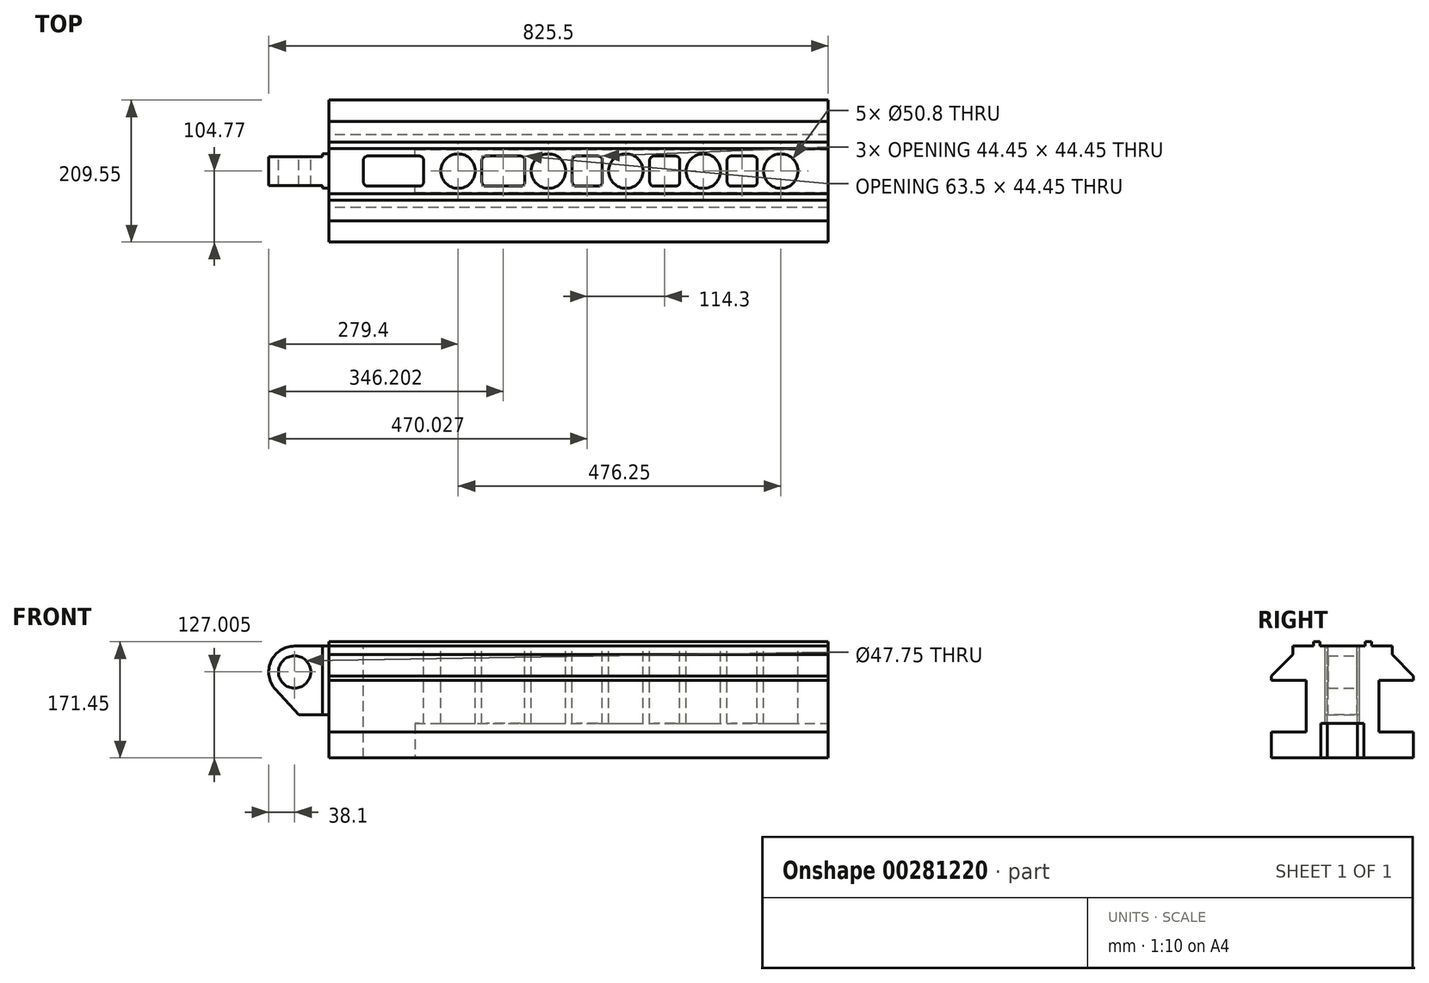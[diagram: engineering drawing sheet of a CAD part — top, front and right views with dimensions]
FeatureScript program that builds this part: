
annotation { "Feature Type Name" : "Feature", "Feature Type Description" : "" }
export const myFeature = defineFeature(function(context is Context, id is Id, definition is map)
    precondition{}
    {
        {
            var Q0;
            Q0=qCreatedBy(makeId("Right.planeOp"),FACE);
            var sketch = newSketch(context, id + "F0", { "sketchPlane" : qUnion([Q0])});
            skLineSegment(sketch, "E0.bottom", {"start": v(-42.8, 85.72) * mm, "end": v(-33.27, 85.72) * mm});
            skLineSegment(sketch, "E0.top", {"start": v(-104.78, -85.73) * mm, "end": v(104.77, -85.73) * mm});
            skLineSegment(sketch, "E0.left", {"start": v(-104.77, 85.72) * mm, "end": v(-104.78, 28.57) * mm});
            skLineSegment(sketch, "E0.right", {"start": v(104.78, 85.72) * mm, "end": v(104.78, 28.58) * mm});
            skPoint(sketch, "E0.middle", {"position": v(0, 0) * mm});
            skLineSegment(sketch, "E1.0", {"start": v(-104.77, 79.38) * mm, "end": v(-42.8, 79.38) * mm});
            skLineSegment(sketch, "E2", {"start": v(0, 110.93) * mm, "end": v(0, 53.07) * mm});
            skLineSegment(sketch, "E3.0", {"start": v(-33.27, 85.72) * mm, "end": v(-33.27, 79.38) * mm});
            skLineSegment(sketch, "E4.0", {"start": v(-42.8, 85.72) * mm, "end": v(-42.8, 79.38) * mm});
            skLineSegment(sketch, "E5.MirrorCS", {"start": v(42.8, 85.72) * mm, "end": v(42.8, 79.38) * mm});
            skLineSegment(sketch, "E6.MirrorCS", {"start": v(33.27, 85.72) * mm, "end": v(33.27, 79.38) * mm});
            skPoint(sketch, "E7.orphan", {"position": v(-42.8, 53.07) * mm});
            skPoint(sketch, "E8.orphan", {"position": v(-33.27, 53.07) * mm});
            skPoint(sketch, "E9.orphan", {"position": v(33.27, 53.07) * mm});
            skPoint(sketch, "E10.orphan", {"position": v(42.8, 53.07) * mm});
            skLineSegment(sketch, "E11.trimOffspring", {"start": v(33.27, 85.72) * mm, "end": v(42.8, 85.72) * mm});
            skPoint(sketch, "E12.orphan", {"position": v(-33.27, 110.93) * mm});
            skPoint(sketch, "E13.orphan", {"position": v(-42.8, 110.93) * mm});
            skPoint(sketch, "E14.orphan", {"position": v(33.27, 110.93) * mm});
            skPoint(sketch, "E15.orphan", {"position": v(42.8, 110.93) * mm});
            skLineSegment(sketch, "E16.trimOffspring", {"start": v(42.8, 79.38) * mm, "end": v(104.78, 79.38) * mm});
            skLineSegment(sketch, "E17.trimOffspring", {"start": v(-33.27, 79.38) * mm, "end": v(33.27, 79.38) * mm});
            skLineSegment(sketch, "E18.0", {"start": v(42.8, 28.57) * mm, "end": v(104.78, 28.57) * mm});
            skLineSegment(sketch, "E19.0", {"start": v(42.8, -47.62) * mm, "end": v(104.78, -47.62) * mm});
            skLineSegment(sketch, "E20.0", {"start": v(53.85, 28.57) * mm, "end": v(53.85, -47.62) * mm});
            skLineSegment(sketch, "E21.trimOffspring", {"start": v(104.77, -47.62) * mm, "end": v(104.77, -85.73) * mm});
            skLineSegment(sketch, "E22.MirrorCS", {"start": v(-42.8, -47.62) * mm, "end": v(-104.78, -47.62) * mm});
            skLineSegment(sketch, "E23.MirrorCS", {"start": v(-42.8, 28.57) * mm, "end": v(-104.78, 28.57) * mm});
            skLineSegment(sketch, "E24.MirrorCS", {"start": v(-53.85, 28.57) * mm, "end": v(-53.85, -47.62) * mm});
            skLineSegment(sketch, "E25.trimOffspring", {"start": v(-104.78, -47.62) * mm, "end": v(-104.78, -85.73) * mm});
            skSolve(sketch);
        }
        {
            var Q0;
            Q0 = qSketchRegion(id + "F0", true);
            extrude(context, id + "F1", {"entities" : qUnion([Q0]), "endBound" : BoundingType.SYMMETRIC, "depth" : 736.6 * mm});
        }
        {
            var Q0;
            Q0=makeQuery(id+"F1.opExtrude","CAP_FACE",FACE,{"disambiguationData":[OSD([sQuery(id+"F0.wireOp",EDGE,"E0.bottom"),sQuery(id+"F0.wireOp",EDGE,"E0.top"),sQuery(id+"F0.wireOp",EDGE,"E0.left"),sQuery(id+"F0.wireOp",EDGE,"E0.right"),sQuery(id+"F0.wireOp",EDGE,"E1.0"),sQuery(id+"F0.wireOp",EDGE,"E3.0"),sQuery(id+"F0.wireOp",EDGE,"E4.0"),sQuery(id+"F0.wireOp",EDGE,"E5.MirrorCS"),sQuery(id+"F0.wireOp",EDGE,"E6.MirrorCS"),sQuery(id+"F0.wireOp",EDGE,"E11.trimOffspring"),sQuery(id+"F0.wireOp",EDGE,"E16.trimOffspring"),sQuery(id+"F0.wireOp",EDGE,"E17.trimOffspring"),sQuery(id+"F0.wireOp",EDGE,"E18.0"),sQuery(id+"F0.wireOp",EDGE,"E19.0"),sQuery(id+"F0.wireOp",EDGE,"E20.0"),sQuery(id+"F0.wireOp",EDGE,"E21.trimOffspring"),sQuery(id+"F0.wireOp",EDGE,"E22.MirrorCS"),sQuery(id+"F0.wireOp",EDGE,"E23.MirrorCS"),sQuery(id+"F0.wireOp",EDGE,"E24.MirrorCS"),sQuery(id+"F0.wireOp",EDGE,"E25.trimOffspring")])],"isStart":false});
            var sketch = newSketch(context, id + "F2", { "sketchPlane" : qUnion([Q0])});
            skLineSegment(sketch, "E26.0", {"start": v(-104.78, -85.73) * mm, "end": v(104.77, -85.73) * mm, "construction": true});
            skLineSegment(sketch, "E27.bottom", {"start": v(-31.75, -34.93) * mm, "end": v(31.75, -34.93) * mm});
            skLineSegment(sketch, "E27.top", {"start": v(-31.75, -136.53) * mm, "end": v(31.75, -136.53) * mm});
            skLineSegment(sketch, "E27.left", {"start": v(-31.75, -34.93) * mm, "end": v(-31.75, -136.53) * mm});
            skLineSegment(sketch, "E27.right", {"start": v(31.75, -34.93) * mm, "end": v(31.75, -136.53) * mm});
            skPoint(sketch, "E27.middle", {"position": v(0, -85.73) * mm});
            skSolve(sketch);
        }
        {
            var Q0;
            Q0 = qSketchRegion(id + "F2", true);
            extrude(context, id + "F3", {"entities" : qUnion([Q0]), "operationType" : NewBodyOperationType.REMOVE, "oppositeDirection" : true, "depth" : 609.6 * mm});
        }
        {
            var Q0;
            Q0=makeQuery(id+"F1.opExtrude","SWEPT_FACE",FACE,{"disambiguationData":[OSD([sQuery(id+"F0.wireOp",EDGE,"E17.trimOffspring")])]});
            var sketch = newSketch(context, id + "F4", { "sketchPlane" : qUnion([Q0])});
            skLineSegment(sketch, "E28.0", {"start": v(-368.3, -33.27) * mm, "end": v(-368.3, 33.27) * mm, "construction": true});
            skLineSegment(sketch, "E29.0", {"start": v(-177.8, -33.27) * mm, "end": v(-177.8, 33.27) * mm, "construction": true});
            skLineSegment(sketch, "E30.0", {"start": v(-44.45, -33.27) * mm, "end": v(-44.45, 33.27) * mm, "construction": true});
            skLineSegment(sketch, "E31.0", {"start": v(69.85, -33.27) * mm, "end": v(69.85, 33.27) * mm, "construction": true});
            skLineSegment(sketch, "E32.0", {"start": v(184.15, -33.27) * mm, "end": v(184.15, 33.27) * mm, "construction": true});
            skLineSegment(sketch, "E33.0", {"start": v(298.45, -33.27) * mm, "end": v(298.45, 33.27) * mm, "construction": true});
            skLineSegment(sketch, "E34", {"start": v(-368.3, 0) * mm, "end": v(340.6, 0) * mm, "construction": true});
            skPoint(sketch, "E35", {"position": v(-177.8, 0) * mm});
            skPoint(sketch, "E36", {"position": v(-44.45, 0) * mm});
            skPoint(sketch, "E37", {"position": v(69.85, 0) * mm});
            skPoint(sketch, "E38", {"position": v(184.15, 0) * mm});
            skPoint(sketch, "E39", {"position": v(298.45, 0) * mm});
            skSolve(sketch);
        }
        {
            var Q0;
            Q0=sQuery(id+"F4.wireOp",VERTEX,"E35");
            var Q1;
            Q1=sQuery(id+"F4.wireOp",VERTEX,"E36");
            var Q2;
            Q2=sQuery(id+"F4.wireOp",VERTEX,"E37");
            var Q3;
            Q3=sQuery(id+"F4.wireOp",VERTEX,"E38");
            var Q4;
            Q4=sQuery(id+"F4.wireOp",VERTEX,"E39");
            var Q5;
            Q5=makeQuery(id+"F1.opExtrude","SWEPT_BODY",BODY,{"disambiguationData":[OSD([sQuery(id+"F0.wireOp",EDGE,"E0.bottom"),sQuery(id+"F0.wireOp",EDGE,"E0.top"),sQuery(id+"F0.wireOp",EDGE,"E0.left"),sQuery(id+"F0.wireOp",EDGE,"E0.right"),sQuery(id+"F0.wireOp",EDGE,"E1.0"),sQuery(id+"F0.wireOp",EDGE,"E3.0"),sQuery(id+"F0.wireOp",EDGE,"E4.0"),sQuery(id+"F0.wireOp",EDGE,"E5.MirrorCS"),sQuery(id+"F0.wireOp",EDGE,"E6.MirrorCS"),sQuery(id+"F0.wireOp",EDGE,"E11.trimOffspring"),sQuery(id+"F0.wireOp",EDGE,"E16.trimOffspring"),sQuery(id+"F0.wireOp",EDGE,"E17.trimOffspring"),sQuery(id+"F0.wireOp",EDGE,"E18.0"),sQuery(id+"F0.wireOp",EDGE,"E19.0"),sQuery(id+"F0.wireOp",EDGE,"E20.0"),sQuery(id+"F0.wireOp",EDGE,"E21.trimOffspring"),sQuery(id+"F0.wireOp",EDGE,"E22.MirrorCS"),sQuery(id+"F0.wireOp",EDGE,"E23.MirrorCS"),sQuery(id+"F0.wireOp",EDGE,"E24.MirrorCS"),sQuery(id+"F0.wireOp",EDGE,"E25.trimOffspring")])]});
            hole(context, id + "F5", {"style" : HoleStyle.SIMPLE, "endStyle" : HoleEndStyle.THROUGH, "holeDiameter" : 50.8 * mm, "tappedDepth" : 42.34 * mm, "tapClearance" : 3, "startFromSketch" : true, "locations" : qUnion([Q0, Q1, Q2, Q3, Q4]), "scope" : qUnion([Q5])});
        }
        {
            var Q0;
            Q0=makeQuery(id+"F1.opExtrude","SWEPT_FACE",FACE,{"disambiguationData":[OSD([sQuery(id+"F0.wireOp",EDGE,"E17.trimOffspring")])]});
            var sketch = newSketch(context, id + "F6", { "sketchPlane" : qUnion([Q0])});
            skCircle(sketch, "E40.0", {"center": v(-177.8, 0) * mm, "radius": 25.4 * mm, "construction": true});
            skCircle(sketch, "E41.0", {"center": v(-44.45, 0) * mm, "radius": 25.4 * mm, "construction": true});
            skCircle(sketch, "E42.0", {"center": v(69.85, 0) * mm, "radius": 25.4 * mm, "construction": true});
            skCircle(sketch, "E43.0", {"center": v(184.15, 0) * mm, "radius": 25.4 * mm, "construction": true});
            skCircle(sketch, "E44.0", {"center": v(298.45, 0) * mm, "radius": 25.4 * mm, "construction": true});
            skLineSegment(sketch, "E45", {"start": v(298.45, 130.35) * mm, "end": v(298.45, -144.63) * mm, "construction": true});
            skLineSegment(sketch, "E46", {"start": v(184.15, 135.32) * mm, "end": v(184.15, -149.6) * mm, "construction": true});
            skLineSegment(sketch, "E47", {"start": v(0, 0) * mm, "end": v(382.37, 0) * mm, "construction": true});
            skPoint(sketch, "E47.endSnap0", {"position": v(368.3, 0) * mm});
            skLineSegment(sketch, "E48.bottom", {"start": v(225.55, 22.23) * mm, "end": v(257.3, 22.23) * mm});
            skLineSegment(sketch, "E48.top", {"start": v(225.55, -22.23) * mm, "end": v(257.3, -22.23) * mm});
            skLineSegment(sketch, "E48.left", {"start": v(219.2, 15.88) * mm, "end": v(219.2, -15.88) * mm});
            skLineSegment(sketch, "E48.right", {"start": v(263.65, 15.88) * mm, "end": v(263.65, -15.88) * mm});
            skPoint(sketch, "E49.visualSharp", {"position": v(219.2, 22.23) * mm});
            skArc(sketch, "E49.filletArc", {"start": v(225.55, 22.23) * mm, "mid": v(221.06, 20.37) * mm, "end": v(219.2, 15.88) * mm});
            skPoint(sketch, "E50.visualSharp", {"position": v(263.65, 22.23) * mm});
            skArc(sketch, "E50.filletArc", {"start": v(263.65, 15.88) * mm, "mid": v(261.8, 20.37) * mm, "end": v(257.3, 22.23) * mm});
            skPoint(sketch, "E51.visualSharp", {"position": v(263.65, -22.23) * mm});
            skArc(sketch, "E51.filletArc", {"start": v(257.3, -22.23) * mm, "mid": v(261.8, -20.37) * mm, "end": v(263.65, -15.88) * mm});
            skPoint(sketch, "E52.visualSharp", {"position": v(219.2, -22.23) * mm});
            skArc(sketch, "E52.filletArc", {"start": v(219.2, -15.88) * mm, "mid": v(221.06, -20.37) * mm, "end": v(225.55, -22.22) * mm});
            skPoint(sketch, "E53.1.0.0", {"position": v(149.35, 22.23) * mm});
            skPoint(sketch, "E53.1.0.1", {"position": v(149.35, -22.23) * mm});
            skLineSegment(sketch, "E53.1.0.2", {"start": v(149.35, 15.88) * mm, "end": v(149.35, -15.88) * mm});
            skLineSegment(sketch, "E53.1.0.3", {"start": v(104.9, 15.88) * mm, "end": v(104.9, -15.88) * mm});
            skLineSegment(sketch, "E53.1.0.4", {"start": v(111.25, -22.23) * mm, "end": v(143, -22.23) * mm});
            skLineSegment(sketch, "E53.1.0.5", {"start": v(111.25, 22.23) * mm, "end": v(143, 22.23) * mm});
            skPoint(sketch, "E53.1.0.6", {"position": v(104.9, 22.23) * mm});
            skPoint(sketch, "E53.1.0.7", {"position": v(104.9, -22.23) * mm});
            skArc(sketch, "E53.1.0.8", {"start": v(149.35, 15.88) * mm, "mid": v(147.5, 20.37) * mm, "end": v(143, 22.23) * mm});
            skArc(sketch, "E53.1.0.9", {"start": v(104.9, -15.88) * mm, "mid": v(106.76, -20.37) * mm, "end": v(111.25, -22.22) * mm});
            skArc(sketch, "E53.1.0.10", {"start": v(111.25, 22.23) * mm, "mid": v(106.76, 20.37) * mm, "end": v(104.9, 15.88) * mm});
            skArc(sketch, "E53.1.0.11", {"start": v(143, -22.23) * mm, "mid": v(147.5, -20.37) * mm, "end": v(149.35, -15.88) * mm});
            skPoint(sketch, "E53.2.0.0", {"position": v(35.05, 22.23) * mm});
            skPoint(sketch, "E53.2.0.1", {"position": v(35.05, -22.23) * mm});
            skLineSegment(sketch, "E53.2.0.2", {"start": v(35.05, 15.88) * mm, "end": v(35.05, -15.88) * mm});
            skLineSegment(sketch, "E53.2.0.3", {"start": v(-9.4, 15.88) * mm, "end": v(-9.4, -15.88) * mm});
            skLineSegment(sketch, "E53.2.0.4", {"start": v(-3.05, -22.23) * mm, "end": v(28.7, -22.23) * mm});
            skLineSegment(sketch, "E53.2.0.5", {"start": v(-3.05, 22.23) * mm, "end": v(28.7, 22.23) * mm});
            skPoint(sketch, "E53.2.0.6", {"position": v(-9.4, 22.23) * mm});
            skPoint(sketch, "E53.2.0.7", {"position": v(-9.4, -22.23) * mm});
            skArc(sketch, "E53.2.0.8", {"start": v(35.05, 15.88) * mm, "mid": v(33.2, 20.37) * mm, "end": v(28.7, 22.23) * mm});
            skArc(sketch, "E53.2.0.9", {"start": v(-9.4, -15.88) * mm, "mid": v(-7.54, -20.37) * mm, "end": v(-3.05, -22.22) * mm});
            skArc(sketch, "E53.2.0.10", {"start": v(-3.05, 22.23) * mm, "mid": v(-7.54, 20.37) * mm, "end": v(-9.4, 15.88) * mm});
            skArc(sketch, "E53.2.0.11", {"start": v(28.7, -22.23) * mm, "mid": v(33.2, -20.37) * mm, "end": v(35.05, -15.88) * mm});
            skPoint(sketch, "E53.3.0.0", {"position": v(-79.25, 22.23) * mm});
            skPoint(sketch, "E53.3.0.1", {"position": v(-79.25, -22.23) * mm});
            skLineSegment(sketch, "E53.3.0.2", {"start": v(-79.25, 15.88) * mm, "end": v(-79.25, -15.87) * mm});
            skLineSegment(sketch, "E53.3.0.3", {"start": v(-142.75, 15.88) * mm, "end": v(-142.75, -15.88) * mm});
            skLineSegment(sketch, "E53.3.0.4", {"start": v(-136.4, -22.22) * mm, "end": v(-85.6, -22.22) * mm});
            skLineSegment(sketch, "E53.3.0.5", {"start": v(-136.4, 22.23) * mm, "end": v(-85.6, 22.23) * mm});
            skPoint(sketch, "E53.3.0.6", {"position": v(-123.7, 22.23) * mm});
            skPoint(sketch, "E53.3.0.7", {"position": v(-123.7, -22.23) * mm});
            skArc(sketch, "E53.3.0.9", {"start": v(-142.75, -15.88) * mm, "mid": v(-140.89, -20.37) * mm, "end": v(-136.4, -22.22) * mm});
            skArc(sketch, "E53.3.0.10", {"start": v(-136.4, 22.23) * mm, "mid": v(-140.89, 20.37) * mm, "end": v(-142.75, 15.88) * mm});
            skPoint(sketch, "E53.4.0.0", {"position": v(-193.55, 22.23) * mm});
            skPoint(sketch, "E53.4.0.1", {"position": v(-193.55, -22.23) * mm});
            skLineSegment(sketch, "E53.4.0.2", {"start": v(-228.6, 15.88) * mm, "end": v(-228.6, -15.88) * mm});
            skLineSegment(sketch, "E53.4.0.3", {"start": v(-317.5, 15.87) * mm, "end": v(-317.5, -15.88) * mm});
            skLineSegment(sketch, "E53.4.0.4", {"start": v(-311.15, -22.22) * mm, "end": v(-234.95, -22.22) * mm});
            skLineSegment(sketch, "E53.4.0.5", {"start": v(-311.15, 22.22) * mm, "end": v(-234.95, 22.22) * mm});
            skPoint(sketch, "E53.4.0.6", {"position": v(-238, 22.23) * mm});
            skPoint(sketch, "E53.4.0.7", {"position": v(-238, -22.23) * mm});
            skArc(sketch, "E53.4.0.9", {"start": v(-317.5, -15.88) * mm, "mid": v(-315.64, -20.37) * mm, "end": v(-311.15, -22.22) * mm});
            skArc(sketch, "E53.4.0.10", {"start": v(-311.15, 22.22) * mm, "mid": v(-315.64, 20.37) * mm, "end": v(-317.5, 15.87) * mm});
            skLineSegment(sketch, "E53.direction1", {"start": v(263.65, 22.23) * mm, "end": v(149.35, 22.23) * mm, "construction": true});
            skArc(sketch, "E54.filletArc", {"start": v(-79.25, 15.88) * mm, "mid": v(-81.1, 20.37) * mm, "end": v(-85.6, 22.23) * mm});
            skPoint(sketch, "E55.visualSharp", {"position": v(-79.25, -22.22) * mm});
            skArc(sketch, "E55.filletArc", {"start": v(-85.6, -22.22) * mm, "mid": v(-81.1, -20.37) * mm, "end": v(-79.25, -15.87) * mm});
            skPoint(sketch, "E56.visualSharp", {"position": v(-228.6, 22.22) * mm});
            skArc(sketch, "E56.filletArc", {"start": v(-228.6, 15.88) * mm, "mid": v(-230.46, 20.37) * mm, "end": v(-234.95, 22.22) * mm});
            skPoint(sketch, "E57.visualSharp", {"position": v(-228.6, -22.22) * mm});
            skArc(sketch, "E57.filletArc", {"start": v(-234.95, -22.23) * mm, "mid": v(-230.46, -20.37) * mm, "end": v(-228.6, -15.88) * mm});
            skSolve(sketch);
        }
        {
            var Q0;
            Q0 = qSketchRegion(id + "F6", true);
            extrude(context, id + "F7", {"entities" : qUnion([Q0]), "operationType" : NewBodyOperationType.REMOVE, "endBound" : BoundingType.THROUGH_ALL, "oppositeDirection" : true, "depth" : 25.4 * mm});
        }
        {
            var Q0;
            Q0=makeQuery(id+"F1.opExtrude","CAP_FACE",FACE,{"disambiguationData":[OSD([sQuery(id+"F0.wireOp",EDGE,"E0.bottom"),sQuery(id+"F0.wireOp",EDGE,"E0.top"),sQuery(id+"F0.wireOp",EDGE,"E0.left"),sQuery(id+"F0.wireOp",EDGE,"E0.right"),sQuery(id+"F0.wireOp",EDGE,"E1.0"),sQuery(id+"F0.wireOp",EDGE,"E3.0"),sQuery(id+"F0.wireOp",EDGE,"E4.0"),sQuery(id+"F0.wireOp",EDGE,"E5.MirrorCS"),sQuery(id+"F0.wireOp",EDGE,"E6.MirrorCS"),sQuery(id+"F0.wireOp",EDGE,"E11.trimOffspring"),sQuery(id+"F0.wireOp",EDGE,"E16.trimOffspring"),sQuery(id+"F0.wireOp",EDGE,"E17.trimOffspring"),sQuery(id+"F0.wireOp",EDGE,"E18.0"),sQuery(id+"F0.wireOp",EDGE,"E19.0"),sQuery(id+"F0.wireOp",EDGE,"E20.0"),sQuery(id+"F0.wireOp",EDGE,"E21.trimOffspring"),sQuery(id+"F0.wireOp",EDGE,"E22.MirrorCS"),sQuery(id+"F0.wireOp",EDGE,"E23.MirrorCS"),sQuery(id+"F0.wireOp",EDGE,"E24.MirrorCS"),sQuery(id+"F0.wireOp",EDGE,"E25.trimOffspring")])],"isStart":false});
            var sketch = newSketch(context, id + "F8", { "sketchPlane" : qUnion([Q0])});
            skLineSegment(sketch, "E58", {"start": v(0, 182.5) * mm, "end": v(0, -180.71) * mm, "construction": true});
            skPoint(sketch, "E58.endSnap0", {"position": v(0, -34.93) * mm});
            skLineSegment(sketch, "E59.0", {"start": v(-73.15, 182.5) * mm, "end": v(-73.15, -180.71) * mm, "construction": true});
            skLineSegment(sketch, "E60.0", {"start": v(-104.77, 66.67) * mm, "end": v(-42.8, 66.67) * mm, "construction": true});
            skLineSegment(sketch, "E61", {"start": v(-73.15, 66.67) * mm, "end": v(-123, 16.84) * mm});
            skLineSegment(sketch, "E62", {"start": v(-73.15, 66.67) * mm, "end": v(-73.15, 82.75) * mm});
            skLineSegment(sketch, "E63", {"start": v(-73.15, 82.75) * mm, "end": v(-119.21, 82.75) * mm});
            skLineSegment(sketch, "E64", {"start": v(-119.21, 82.75) * mm, "end": v(-119.21, 15.31) * mm});
            skLineSegment(sketch, "E65.MirrorCS", {"start": v(73.15, 66.67) * mm, "end": v(73.15, 82.75) * mm});
            skLineSegment(sketch, "E66.MirrorCS", {"start": v(119.21, 82.75) * mm, "end": v(119.21, 15.31) * mm});
            skLineSegment(sketch, "E67.MirrorCS", {"start": v(73.15, 82.75) * mm, "end": v(119.21, 82.75) * mm});
            skLineSegment(sketch, "E68.MirrorCS", {"start": v(73.15, 66.67) * mm, "end": v(123, 16.84) * mm});
            skSolve(sketch);
        }
        {
            var Q0;
            Q0 = qSketchRegion(id + "F8", true);
            extrude(context, id + "F9", {"entities" : qUnion([Q0]), "operationType" : NewBodyOperationType.REMOVE, "endBound" : BoundingType.THROUGH_ALL, "oppositeDirection" : true, "depth" : 25.4 * mm});
        }
        {
            var Q0;
            Q0=makeQuery(id+"F1.opExtrude","CAP_FACE",FACE,{"disambiguationData":[OSD([sQuery(id+"F0.wireOp",EDGE,"E0.bottom"),sQuery(id+"F0.wireOp",EDGE,"E0.top"),sQuery(id+"F0.wireOp",EDGE,"E0.left"),sQuery(id+"F0.wireOp",EDGE,"E0.right"),sQuery(id+"F0.wireOp",EDGE,"E1.0"),sQuery(id+"F0.wireOp",EDGE,"E3.0"),sQuery(id+"F0.wireOp",EDGE,"E4.0"),sQuery(id+"F0.wireOp",EDGE,"E5.MirrorCS"),sQuery(id+"F0.wireOp",EDGE,"E6.MirrorCS"),sQuery(id+"F0.wireOp",EDGE,"E11.trimOffspring"),sQuery(id+"F0.wireOp",EDGE,"E16.trimOffspring"),sQuery(id+"F0.wireOp",EDGE,"E17.trimOffspring"),sQuery(id+"F0.wireOp",EDGE,"E18.0"),sQuery(id+"F0.wireOp",EDGE,"E19.0"),sQuery(id+"F0.wireOp",EDGE,"E20.0"),sQuery(id+"F0.wireOp",EDGE,"E21.trimOffspring"),sQuery(id+"F0.wireOp",EDGE,"E22.MirrorCS"),sQuery(id+"F0.wireOp",EDGE,"E23.MirrorCS"),sQuery(id+"F0.wireOp",EDGE,"E24.MirrorCS"),sQuery(id+"F0.wireOp",EDGE,"E25.trimOffspring")])],"isStart":true});
            var sketch = newSketch(context, id + "F10", { "sketchPlane" : qUnion([Q0])});
            skLineSegment(sketch, "E69.0", {"start": v(33.27, 79.38) * mm, "end": v(-33.27, 79.38) * mm, "construction": true});
            skLineSegment(sketch, "E70.0", {"start": v(33.27, 28.57) * mm, "end": v(-33.27, 28.57) * mm, "construction": true});
            skLineSegment(sketch, "E71.bottom", {"start": v(-25.4, 79.38) * mm, "end": v(25.4, 79.38) * mm});
            skLineSegment(sketch, "E71.top", {"start": v(-25.4, -22.23) * mm, "end": v(25.4, -22.23) * mm});
            skLineSegment(sketch, "E71.left", {"start": v(-25.4, 79.38) * mm, "end": v(-25.4, -22.23) * mm});
            skLineSegment(sketch, "E71.right", {"start": v(25.4, 79.38) * mm, "end": v(25.4, -22.23) * mm});
            skPoint(sketch, "E71.middle", {"position": v(0, 28.57) * mm});
            skSolve(sketch);
        }
        {
            var Q0;
            Q0 = qSketchRegion(id + "F10", true);
            extrude(context, id + "F11", {"entities" : qUnion([Q0]), "depth" : 88.9 * mm});
        }
        {
            var Q0;
            Q0=makeQuery(id+"F11.opExtrude","SWEPT_FACE",FACE,{"disambiguationData":[OSD([sQuery(id+"F10.wireOp",EDGE,"E71.bottom")])]});
            var sketch = newSketch(context, id + "F12", { "sketchPlane" : qUnion([Q0])});
            skLineSegment(sketch, "E72.0", {"start": v(-377.95, -25.4) * mm, "end": v(-377.95, -21.44) * mm});
            skLineSegment(sketch, "E73", {"start": v(-333.3, 0) * mm, "end": v(-480.5, 0) * mm});
            skLineSegment(sketch, "E74.0", {"start": v(-377.95, 21.44) * mm, "end": v(-457.2, 21.44) * mm});
            skLineSegment(sketch, "E75.0", {"start": v(-457.2, 25.4) * mm, "end": v(-377.95, 25.4) * mm});
            skLineSegment(sketch, "E76.0", {"start": v(-457.2, -25.4) * mm, "end": v(-457.2, 0) * mm});
            skLineSegment(sketch, "E77.trimOffspring", {"start": v(-377.95, 21.44) * mm, "end": v(-377.95, 25.4) * mm});
            skPoint(sketch, "E78.orphan", {"position": v(-368.3, 25.4) * mm});
            skLineSegment(sketch, "E79.trimOffspring", {"start": v(-457.2, 21.44) * mm, "end": v(-457.2, 25.4) * mm});
            skLineSegment(sketch, "E80.MirrorCS", {"start": v(-457.2, -21.44) * mm, "end": v(-457.2, -25.4) * mm});
            skLineSegment(sketch, "E81.MirrorCS", {"start": v(-377.95, -21.44) * mm, "end": v(-377.95, -25.4) * mm});
            skPoint(sketch, "E82.MirrorP", {"position": v(-368.3, -25.4) * mm});
            skLineSegment(sketch, "E83.MirrorCS", {"start": v(-377.95, -21.44) * mm, "end": v(-457.2, -21.44) * mm});
            skLineSegment(sketch, "E84.MirrorCS", {"start": v(-457.2, -25.4) * mm, "end": v(-377.95, -25.4) * mm});
            skSolve(sketch);
        }
        {
            var Q0;
            Q0 = qSketchRegion(id + "F12", true);
            extrude(context, id + "F13", {"entities" : qUnion([Q0]), "operationType" : NewBodyOperationType.REMOVE, "endBound" : BoundingType.THROUGH_ALL, "oppositeDirection" : true, "depth" : 25.4 * mm});
        }
        {
            var Q0;
            Q0=makeQuery(id+"F13.boolean.opBoolean","COPY",FACE,{"derivedFrom":makeQuery(id+"F13.opExtrude","SWEPT_FACE",FACE,{"disambiguationData":[OSD([sQuery(id+"F12.wireOp",EDGE,"E74.0")])]})});
            var sketch = newSketch(context, id + "F14", { "sketchPlane" : qUnion([Q0])});
            skLineSegment(sketch, "E85.0", {"start": v(419.1, 79.38) * mm, "end": v(419.1, -22.22) * mm, "construction": true});
            skLineSegment(sketch, "E86.0", {"start": v(377.95, 41.27) * mm, "end": v(457.2, 41.27) * mm, "construction": true});
            skCircle(sketch, "E87", {"center": v(419.1, 41.27) * mm, "radius": 23.88 * mm});
            skSolve(sketch);
        }
        {
            var Q0;
            Q0 = qSketchRegion(id + "F14", true);
            extrude(context, id + "F15", {"entities" : qUnion([Q0]), "operationType" : NewBodyOperationType.REMOVE, "endBound" : BoundingType.THROUGH_ALL, "oppositeDirection" : true, "depth" : 25.4 * mm});
        }
        {
            var Q0;
            Q0=makeQuery(id+"F13.boolean.opBoolean","COPY",FACE,{"derivedFrom":makeQuery(id+"F13.opExtrude","SWEPT_FACE",FACE,{"disambiguationData":[OSD([sQuery(id+"F12.wireOp",EDGE,"E74.0")])]})});
            var sketch = newSketch(context, id + "F16", { "sketchPlane" : qUnion([Q0])});
            skCircle(sketch, "E88.0", {"center": v(419.1, 41.27) * mm, "radius": 23.88 * mm, "construction": true});
            skLineSegment(sketch, "E89.0", {"start": v(412.75, 79.38) * mm, "end": v(412.75, -22.22) * mm, "construction": true});
            skArc(sketch, "E90", {"start": v(447.25, 15.6) * mm, "mid": v(453.96, 56.66) * mm, "end": v(419.1, 79.38) * mm});
            skLineSegment(sketch, "E91", {"start": v(419.1, 79.38) * mm, "end": v(419.1, 99.69) * mm});
            skLineSegment(sketch, "E92", {"start": v(412.75, -22.22) * mm, "end": v(447.25, 15.6) * mm});
            skLineSegment(sketch, "E93", {"start": v(412.75, -22.22) * mm, "end": v(412.75, -37.57) * mm});
            skLineSegment(sketch, "E94", {"start": v(412.75, -37.57) * mm, "end": v(486.45, -37.57) * mm});
            skLineSegment(sketch, "E95", {"start": v(486.45, -37.57) * mm, "end": v(486.45, 99.69) * mm});
            skLineSegment(sketch, "E96", {"start": v(486.45, 99.69) * mm, "end": v(419.1, 99.69) * mm});
            skSolve(sketch);
        }
        {
            var Q0;
            Q0 = qSketchRegion(id + "F16", true);
            extrude(context, id + "F17", {"entities" : qUnion([Q0]), "operationType" : NewBodyOperationType.REMOVE, "endBound" : BoundingType.THROUGH_ALL, "oppositeDirection" : true, "depth" : 25.4 * mm});
        }
    });
